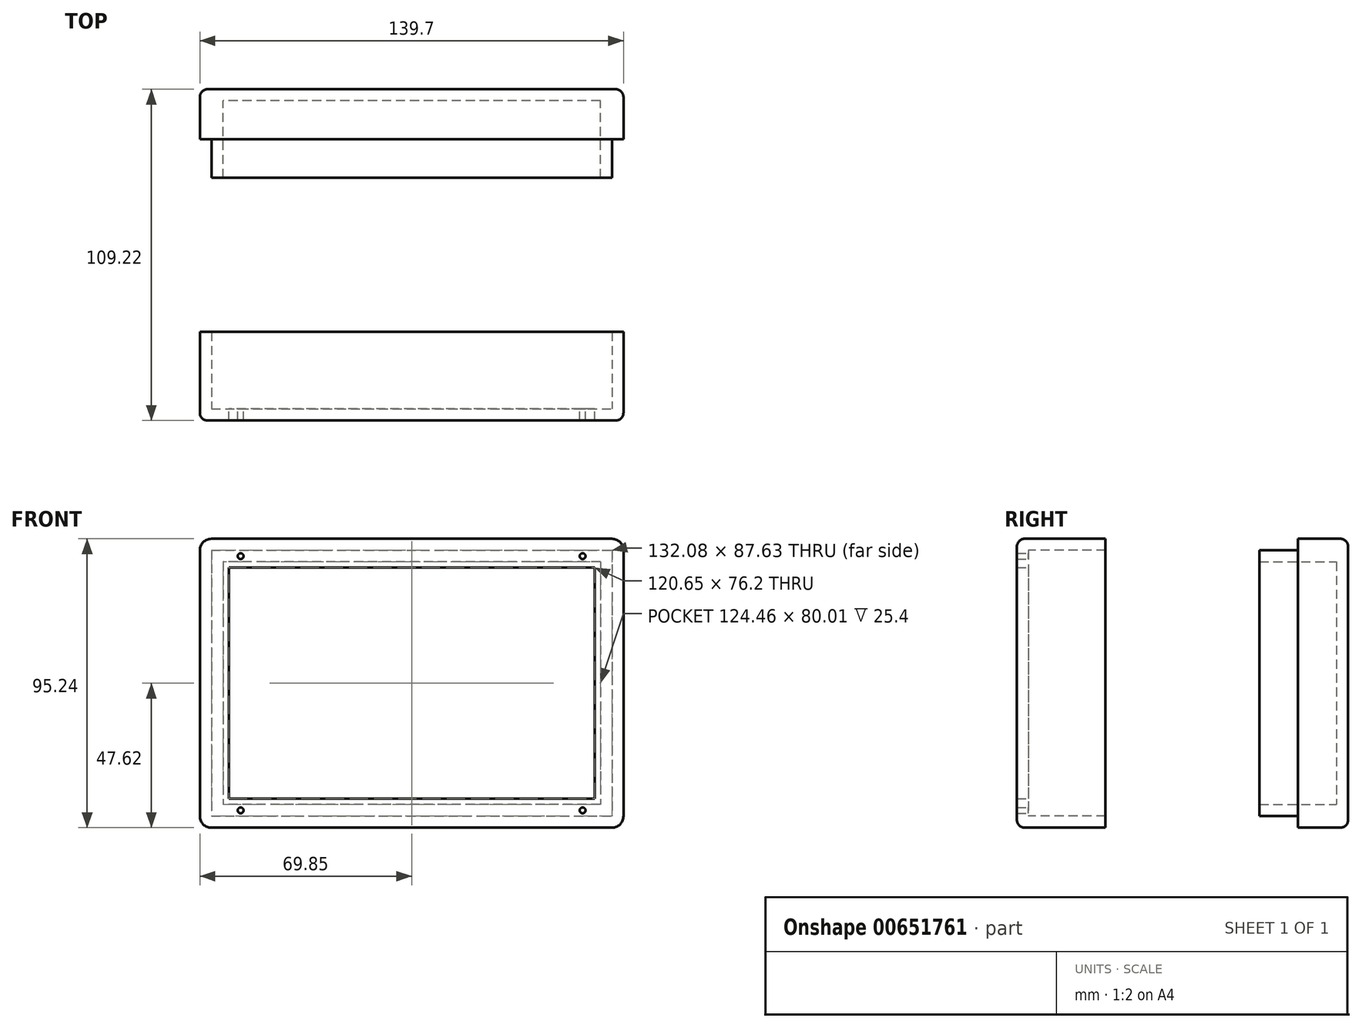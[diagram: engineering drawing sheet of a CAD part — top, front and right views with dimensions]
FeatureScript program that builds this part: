
annotation { "Feature Type Name" : "Feature", "Feature Type Description" : "" }
export const myFeature = defineFeature(function(context is Context, id is Id, definition is map)
    precondition{}
    {
        {
            var Q0;
            Q0=qCreatedBy(makeId("Front.planeOp"),FACE);
            var sketch = newSketch(context, id + "F0", { "sketchPlane" : qUnion([Q0])});
            skPoint(sketch, "E0.middle", {"position": v(0, 0) * mm});
            skLineSegment(sketch, "E1.bottom", {"start": v(60.33, 38.1) * mm, "end": v(-60.33, 38.1) * mm});
            skLineSegment(sketch, "E1.top", {"start": v(60.33, -38.1) * mm, "end": v(-60.32, -38.1) * mm});
            skLineSegment(sketch, "E1.left", {"start": v(60.32, 38.1) * mm, "end": v(60.33, -38.1) * mm});
            skLineSegment(sketch, "E1.right", {"start": v(-60.33, 38.1) * mm, "end": v(-60.32, -38.1) * mm});
            skCircle(sketch, "E2", {"center": v(-56.39, 41.91) * mm, "radius": 0.95 * mm});
            skCircle(sketch, "E3", {"center": v(56.39, 41.91) * mm, "radius": 0.95 * mm});
            skCircle(sketch, "E4", {"center": v(-56.39, -41.91) * mm, "radius": 0.95 * mm});
            skCircle(sketch, "E5", {"center": v(56.39, -41.91) * mm, "radius": 0.95 * mm});
            skLineSegment(sketch, "E6.bottom", {"start": v(69.85, 47.63) * mm, "end": v(-69.85, 47.63) * mm});
            skLineSegment(sketch, "E6.top", {"start": v(69.85, -47.62) * mm, "end": v(-69.85, -47.63) * mm});
            skLineSegment(sketch, "E6.left", {"start": v(69.85, 47.63) * mm, "end": v(69.85, -47.63) * mm});
            skLineSegment(sketch, "E6.right", {"start": v(-69.85, 47.63) * mm, "end": v(-69.85, -47.63) * mm});
            skSolve(sketch);
        }
        {
            var Q0;
            Q0=makeQuery(id+"F0.imprint","IMPRINT",FACE,{"disambiguationData":[TD([[makeQuery(id+"F0.imprint","IMPRINT",EDGE,{"derivedFrom":sQuery(id+"F0.wireOp",EDGE,"E1.bottom")}),-1.0]])]});
            extrude(context, id + "F1", {"entities" : qUnion([Q0]), "depth" : 3.8 * mm, "offsetDistance" : 25.4 * mm});
        }
        {
            var Q0;
            Q0=makeQuery(id+"F1.opExtrude","CAP_FACE",FACE,{"disambiguationData":[OSD([sQuery(id+"F0.wireOp",EDGE,"E1.bottom"),sQuery(id+"F0.wireOp",EDGE,"E1.top"),sQuery(id+"F0.wireOp",EDGE,"E1.left"),sQuery(id+"F0.wireOp",EDGE,"E1.right"),sQuery(id+"F0.wireOp",EDGE,"E2"),sQuery(id+"F0.wireOp",EDGE,"E3"),sQuery(id+"F0.wireOp",EDGE,"E4"),sQuery(id+"F0.wireOp",EDGE,"E5"),sQuery(id+"F0.wireOp",EDGE,"E6.bottom"),sQuery(id+"F0.wireOp",EDGE,"E6.top"),sQuery(id+"F0.wireOp",EDGE,"E6.left"),sQuery(id+"F0.wireOp",EDGE,"E6.right")])],"isStart":true});
            var sketch = newSketch(context, id + "F2", { "sketchPlane" : qUnion([Q0])});
            skLineSegment(sketch, "E7.bottom", {"start": v(66.04, 43.82) * mm, "end": v(-66.04, 43.82) * mm});
            skLineSegment(sketch, "E7.top", {"start": v(66.04, -43.82) * mm, "end": v(-66.04, -43.82) * mm});
            skLineSegment(sketch, "E7.left", {"start": v(66.04, 43.82) * mm, "end": v(66.04, -43.82) * mm});
            skLineSegment(sketch, "E7.right", {"start": v(-66.04, 43.82) * mm, "end": v(-66.04, -43.82) * mm});
            skPoint(sketch, "E7.middle", {"position": v(0, 0) * mm});
            skLineSegment(sketch, "E8.bottom", {"start": v(-69.85, 47.63) * mm, "end": v(69.85, 47.63) * mm});
            skLineSegment(sketch, "E8.top", {"start": v(-69.85, -47.63) * mm, "end": v(69.85, -47.63) * mm});
            skLineSegment(sketch, "E8.left", {"start": v(-69.85, 47.63) * mm, "end": v(-69.85, -47.63) * mm});
            skLineSegment(sketch, "E8.right", {"start": v(69.85, 47.63) * mm, "end": v(69.85, -47.63) * mm});
            skSolve(sketch);
        }
        {
            var Q0;
            Q0=makeQuery(id+"F2.imprint","IMPRINT",FACE,{"disambiguationData":[TD([[makeQuery(id+"F2.imprint","IMPRINT",EDGE,{"derivedFrom":sQuery(id+"F2.wireOp",EDGE,"E7.bottom")}),-1.0]])]});
            extrude(context, id + "F3", {"entities" : qUnion([Q0]), "operationType" : NewBodyOperationType.ADD, "depth" : 25.4 * mm, "offsetDistance" : 25.4 * mm});
        }
        {
            var Q0;
            Q0=makeQuery(id+"F3.boolean.opBoolean","MERGE",EDGE,{"derivedFrom":[makeQuery(id+"F1.opExtrude","SWEPT_EDGE",EDGE,{"disambiguationData":[OSD([sQuery(id+"F0.wireOp",EDGE,"E6.bottom"),sQuery(id+"F0.wireOp",EDGE,"E6.left")])]}),makeQuery(id+"F3.opExtrude","SWEPT_EDGE",EDGE,{"disambiguationData":[OSD([sQuery(id+"F2.wireOp",EDGE,"E8.bottom"),sQuery(id+"F2.wireOp",EDGE,"E8.left")])]})]});
            var Q1;
            Q1=makeQuery(id+"F3.boolean.opBoolean","MERGE",EDGE,{"derivedFrom":[makeQuery(id+"F1.opExtrude","SWEPT_EDGE",EDGE,{"disambiguationData":[OSD([sQuery(id+"F0.wireOp",EDGE,"E6.bottom"),sQuery(id+"F0.wireOp",EDGE,"E6.right")])]}),makeQuery(id+"F3.opExtrude","SWEPT_EDGE",EDGE,{"disambiguationData":[OSD([sQuery(id+"F2.wireOp",EDGE,"E8.bottom"),sQuery(id+"F2.wireOp",EDGE,"E8.right")])]})]});
            var Q2;
            Q2=makeQuery(id+"F3.boolean.opBoolean","MERGE",EDGE,{"derivedFrom":[makeQuery(id+"F1.opExtrude","SWEPT_EDGE",EDGE,{"disambiguationData":[OSD([sQuery(id+"F0.wireOp",EDGE,"E6.top"),sQuery(id+"F0.wireOp",EDGE,"E6.left")])]}),makeQuery(id+"F3.opExtrude","SWEPT_EDGE",EDGE,{"disambiguationData":[OSD([sQuery(id+"F2.wireOp",EDGE,"E8.top"),sQuery(id+"F2.wireOp",EDGE,"E8.left")])]})]});
            var Q3;
            Q3=makeQuery(id+"F3.boolean.opBoolean","MERGE",EDGE,{"derivedFrom":[makeQuery(id+"F1.opExtrude","SWEPT_EDGE",EDGE,{"disambiguationData":[OSD([sQuery(id+"F0.wireOp",EDGE,"E6.top"),sQuery(id+"F0.wireOp",EDGE,"E6.right")])]}),makeQuery(id+"F3.opExtrude","SWEPT_EDGE",EDGE,{"disambiguationData":[OSD([sQuery(id+"F2.wireOp",EDGE,"E8.top"),sQuery(id+"F2.wireOp",EDGE,"E8.right")])]})]});
            fillet(context, id + "F4", {"entities" : qUnion([Q0, Q1, Q2, Q3]), "radius" : 3.8 * mm, "tangentPropagation" : true, "allowEdgeOverflow" : false});
        }
        {
            var Q0;
            Q0=makeQuery(id+"F1.opExtrude","CAP_EDGE",EDGE,{"disambiguationData":[OSD([sQuery(id+"F0.wireOp",EDGE,"E6.bottom")])],"isStart":false});
            var Q1;
            Q1=makeQuery(id+"F1.opExtrude","CAP_EDGE",EDGE,{"disambiguationData":[OSD([sQuery(id+"F0.wireOp",EDGE,"E6.left")])],"isStart":false});
            fillet(context, id + "F5", {"entities" : qUnion([Q0, Q1]), "radius" : 2.54 * mm, "tangentPropagation" : true, "allowEdgeOverflow" : false});
        }
        {
            var Q0;
            Q0=qCreatedBy(makeId("Front.planeOp"),FACE);
            cPlane(context, id + "F6", {"entities" : qUnion([Q0]), "cplaneType" : CPlaneType.OFFSET, "offset" : 101.6 * mm, "oppositeDirection" : true, "width" : 152.4 * mm, "height" : 152.4 * mm});
        }
        {
            var Q0;
            Q0=qCreatedBy(id+"F6.planeOp",FACE);
            var sketch = newSketch(context, id + "F7", { "sketchPlane" : qUnion([Q0])});
            skLineSegment(sketch, "E9.bottom", {"start": v(-69.85, 47.63) * mm, "end": v(69.85, 47.63) * mm});
            skLineSegment(sketch, "E9.top", {"start": v(-69.85, -47.63) * mm, "end": v(69.85, -47.63) * mm});
            skLineSegment(sketch, "E9.left", {"start": v(-69.85, 47.63) * mm, "end": v(-69.85, -47.63) * mm});
            skLineSegment(sketch, "E9.right", {"start": v(69.85, 47.63) * mm, "end": v(69.85, -47.63) * mm});
            skPoint(sketch, "E9.middle", {"position": v(0, 0) * mm});
            skLineSegment(sketch, "E10.bottom", {"start": v(-66.04, 43.82) * mm, "end": v(66.04, 43.82) * mm});
            skLineSegment(sketch, "E10.top", {"start": v(-66.04, -43.82) * mm, "end": v(66.04, -43.82) * mm});
            skLineSegment(sketch, "E10.left", {"start": v(-66.04, 43.82) * mm, "end": v(-66.04, -43.82) * mm});
            skLineSegment(sketch, "E10.right", {"start": v(66.04, 43.82) * mm, "end": v(66.04, -43.82) * mm});
            skSolve(sketch);
        }
        {
            var Q0;
            Q0=makeQuery(id+"F7.imprint","IMPRINT",FACE,{"disambiguationData":[TD([[makeQuery(id+"F7.imprint","IMPRINT",EDGE,{"derivedFrom":sQuery(id+"F7.wireOp",EDGE,"E9.bottom")}),-1.0]])]});
            var Q1;
            Q1=makeQuery(id+"F7.imprint","IMPRINT",FACE,{"disambiguationData":[TD([[makeQuery(id+"F7.imprint","IMPRINT",EDGE,{"derivedFrom":sQuery(id+"F7.wireOp",EDGE,"E10.bottom")}),-1.0]])]});
            extrude(context, id + "F8", {"entities" : qUnion([Q0, Q1]), "oppositeDirection" : true, "depth" : 3.8 * mm, "offsetDistance" : 25.4 * mm});
        }
        {
            var Q0;
            Q0=makeQuery(id+"F7.imprint","IMPRINT",FACE,{"disambiguationData":[TD([[makeQuery(id+"F7.imprint","IMPRINT",EDGE,{"derivedFrom":sQuery(id+"F7.wireOp",EDGE,"E9.bottom")}),-1.0]])]});
            extrude(context, id + "F9", {"entities" : qUnion([Q0]), "operationType" : NewBodyOperationType.ADD, "depth" : 12.7 * mm, "offsetDistance" : 25.4 * mm});
        }
        {
            var Q0;
            {var subQ0=sQuery(id+"F7.wireOp",EDGE,"E9.right");var subQ1=sQuery(id+"F7.wireOp",EDGE,"E9.bottom");Q0=makeQuery(id+"F9.boolean.opBoolean","MERGE",EDGE,{"derivedFrom":[makeQuery(id+"F8.opExtrude","SWEPT_EDGE",EDGE,{"disambiguationData":[OSD([subQ1,subQ0])]}),makeQuery(id+"F9.opExtrude","SWEPT_EDGE",EDGE,{"disambiguationData":[OSD([subQ1,subQ0])]})]});}
            var Q1;
            {var subQ0=sQuery(id+"F7.wireOp",EDGE,"E9.left");var subQ1=sQuery(id+"F7.wireOp",EDGE,"E9.bottom");Q1=makeQuery(id+"F9.boolean.opBoolean","MERGE",EDGE,{"derivedFrom":[makeQuery(id+"F8.opExtrude","SWEPT_EDGE",EDGE,{"disambiguationData":[OSD([subQ1,subQ0])]}),makeQuery(id+"F9.opExtrude","SWEPT_EDGE",EDGE,{"disambiguationData":[OSD([subQ1,subQ0])]})]});}
            var Q2;
            {var subQ0=sQuery(id+"F7.wireOp",EDGE,"E9.right");var subQ1=sQuery(id+"F7.wireOp",EDGE,"E9.top");Q2=makeQuery(id+"F9.boolean.opBoolean","MERGE",EDGE,{"derivedFrom":[makeQuery(id+"F8.opExtrude","SWEPT_EDGE",EDGE,{"disambiguationData":[OSD([subQ1,subQ0])]}),makeQuery(id+"F9.opExtrude","SWEPT_EDGE",EDGE,{"disambiguationData":[OSD([subQ1,subQ0])]})]});}
            var Q3;
            {var subQ0=sQuery(id+"F7.wireOp",EDGE,"E9.left");var subQ1=sQuery(id+"F7.wireOp",EDGE,"E9.top");Q3=makeQuery(id+"F9.boolean.opBoolean","MERGE",EDGE,{"derivedFrom":[makeQuery(id+"F8.opExtrude","SWEPT_EDGE",EDGE,{"disambiguationData":[OSD([subQ1,subQ0])]}),makeQuery(id+"F9.opExtrude","SWEPT_EDGE",EDGE,{"disambiguationData":[OSD([subQ1,subQ0])]})]});}
            fillet(context, id + "F10", {"entities" : qUnion([Q0, Q1, Q2, Q3]), "radius" : 3.8 * mm, "tangentPropagation" : true, "allowEdgeOverflow" : false});
        }
        {
            var Q0;
            Q0=makeQuery(id+"F8.opExtrude","CAP_EDGE",EDGE,{"disambiguationData":[OSD([sQuery(id+"F7.wireOp",EDGE,"E9.bottom")])],"isStart":false});
            fillet(context, id + "F11", {"entities" : qUnion([Q0]), "radius" : 2.54 * mm, "tangentPropagation" : true, "allowEdgeOverflow" : false});
        }
        {
            var Q0;
            Q0=makeQuery(id+"F8.opExtrude","CAP_FACE",FACE,{"disambiguationData":[OSD([sQuery(id+"F7.wireOp",EDGE,"E9.bottom"),sQuery(id+"F7.wireOp",EDGE,"E9.top"),sQuery(id+"F7.wireOp",EDGE,"E9.left"),sQuery(id+"F7.wireOp",EDGE,"E9.right")])],"isStart":true});
            var sketch = newSketch(context, id + "F12", { "sketchPlane" : qUnion([Q0])});
            skLineSegment(sketch, "E11.bottom", {"start": v(62.23, 40) * mm, "end": v(-62.23, 40) * mm});
            skLineSegment(sketch, "E11.top", {"start": v(62.23, -40) * mm, "end": v(-62.23, -40) * mm});
            skLineSegment(sketch, "E11.left", {"start": v(62.23, 40) * mm, "end": v(62.23, -40) * mm});
            skLineSegment(sketch, "E11.right", {"start": v(-62.23, 40) * mm, "end": v(-62.23, -40) * mm});
            skPoint(sketch, "E11.middle", {"position": v(0, 0) * mm});
            skLineSegment(sketch, "E12.bottom", {"start": v(66.04, 43.82) * mm, "end": v(-66.04, 43.82) * mm});
            skLineSegment(sketch, "E12.top", {"start": v(66.04, -43.82) * mm, "end": v(-66.04, -43.82) * mm});
            skLineSegment(sketch, "E12.left", {"start": v(66.04, 43.82) * mm, "end": v(66.04, -43.82) * mm});
            skLineSegment(sketch, "E12.right", {"start": v(-66.04, 43.82) * mm, "end": v(-66.04, -43.82) * mm});
            skSolve(sketch);
        }
        {
            var Q0;
            Q0=makeQuery(id+"F12.imprint","IMPRINT",FACE,{"disambiguationData":[TD([[makeQuery(id+"F12.imprint","IMPRINT",EDGE,{"derivedFrom":sQuery(id+"F12.wireOp",EDGE,"E11.bottom")}),-1.0]])]});
            extrude(context, id + "F13", {"entities" : qUnion([Q0]), "operationType" : NewBodyOperationType.ADD, "depth" : 25.4 * mm, "offsetDistance" : 25.4 * mm});
        }
    });
